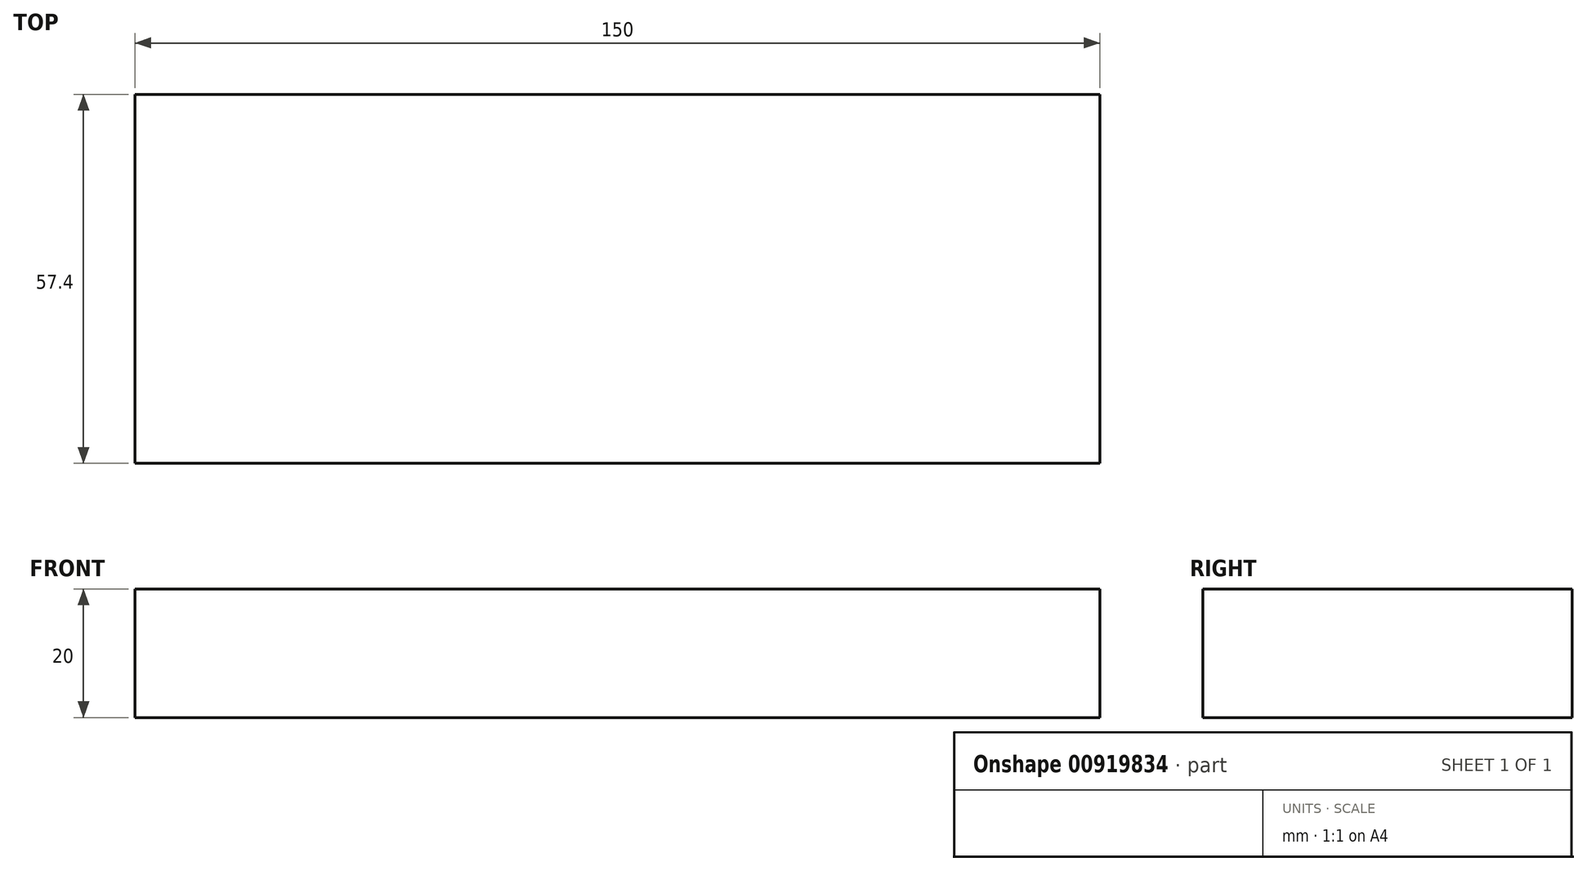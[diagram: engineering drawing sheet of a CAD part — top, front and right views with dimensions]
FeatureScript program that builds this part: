
annotation { "Feature Type Name" : "Feature", "Feature Type Description" : "" }
export const myFeature = defineFeature(function(context is Context, id is Id, definition is map)
    precondition{}
    {
        {
            var Q0;
            Q0=qCreatedBy(makeId("Top.planeOp"),FACE);
            var sketch = newSketch(context, id + "F0", { "sketchPlane" : qUnion([Q0])});
            skLineSegment(sketch, "E0.bottom", {"start": v(75, 28.7) * mm, "end": v(-75, 28.7) * mm});
            skLineSegment(sketch, "E0.top", {"start": v(75, -28.7) * mm, "end": v(-75, -28.7) * mm});
            skLineSegment(sketch, "E0.left", {"start": v(75, 28.7) * mm, "end": v(75, -28.7) * mm});
            skLineSegment(sketch, "E0.right", {"start": v(-75, 28.7) * mm, "end": v(-75, -28.7) * mm});
            skPoint(sketch, "E0.middle", {"position": v(0, 0) * mm});
            skSolve(sketch);
        }
        {
            var Q0;
            Q0 = qSketchRegion(id + "F0", true);
            extrude(context, id + "F1", {"entities" : qUnion([Q0]), "depth" : 20 * mm, "offsetDistance" : 25 * mm});
        }
        {
            var Q0;
            Q0=makeQuery(id+"F1.opExtrude","CAP_FACE",FACE,{"disambiguationData":[OSD([sQuery(id+"F0.wireOp",EDGE,"E0.bottom"),sQuery(id+"F0.wireOp",EDGE,"E0.top"),sQuery(id+"F0.wireOp",EDGE,"E0.left"),sQuery(id+"F0.wireOp",EDGE,"E0.right")])],"isStart":false});
            var sketch = newSketch(context, id + "F2", { "sketchPlane" : qUnion([Q0])});
            skCircle(sketch, "E1", {"center": v(-60.8, 0) * mm, "radius": 10 * mm});
            skCircle(sketch, "E2", {"center": v(-35.8, 0) * mm, "radius": 10 * mm});
            skSolve(sketch);
        }
        {
            var Q0;
            Q0=makeQuery(id+"F2.imprint","IMPRINT",FACE,{"disambiguationData":[TD([[makeQuery(id+"F2.imprint","IMPRINT",EDGE,{"derivedFrom":sQuery(id+"F2.wireOp",EDGE,"E1")}),-1.0]])]});
            cPlane(context, id + "F3", {"entities" : qUnion([Q0]), "cplaneType" : CPlaneType.OFFSET, "offset" : 20 * mm, "width" : 150 * mm, "height" : 150 * mm});
        }
    });
